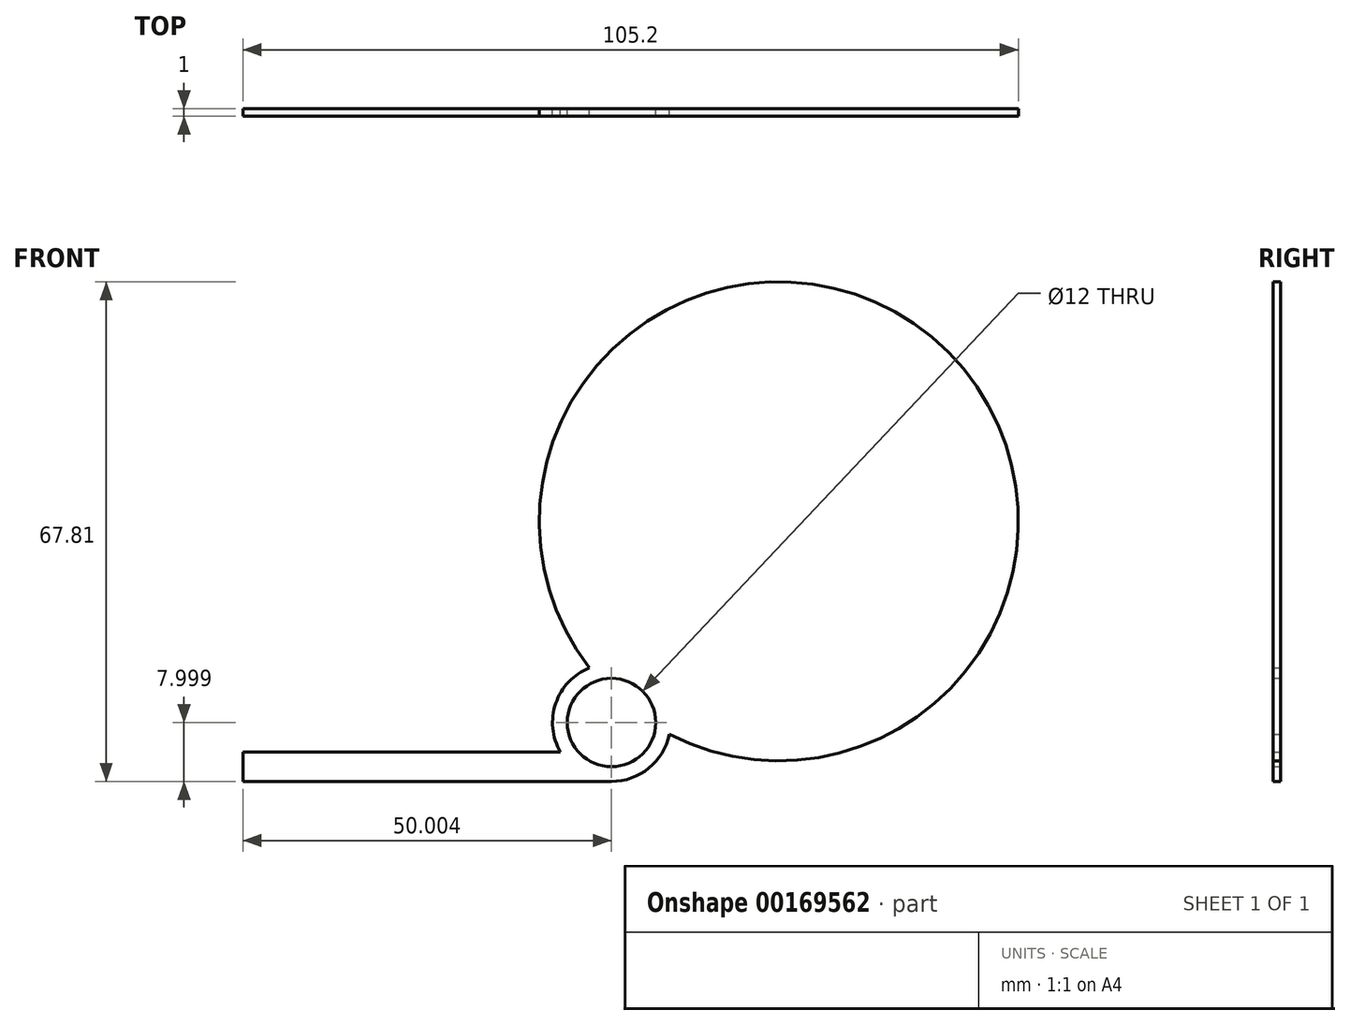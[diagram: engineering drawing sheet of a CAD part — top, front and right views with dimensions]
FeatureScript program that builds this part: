
annotation { "Feature Type Name" : "Feature", "Feature Type Description" : "" }
export const myFeature = defineFeature(function(context is Context, id is Id, definition is map)
    precondition{}
    {
        {
            var Q0;
            Q0=qCreatedBy(makeId("Front.planeOp"),FACE);
            var sketch = newSketch(context, id + "F0", { "sketchPlane" : qUnion([Q0])});
            skCircle(sketch, "E0", {"center": v(0, 0) * mm, "radius": 32.5 * mm});
            skLineSegment(sketch, "E1.bottom", {"start": v(-72.7, -31.31) * mm, "end": v(-22.7, -31.31) * mm});
            skLineSegment(sketch, "E1.top", {"start": v(-72.7, -35.31) * mm, "end": v(-22.7, -35.31) * mm});
            skLineSegment(sketch, "E1.left", {"start": v(-72.7, -31.31) * mm, "end": v(-72.7, -35.31) * mm});
            skLineSegment(sketch, "E1.right", {"start": v(-22.7, -31.31) * mm, "end": v(-22.7, -35.31) * mm});
            skLineSegment(sketch, "E2", {"start": v(0, 0) * mm, "end": v(-17.5, -30.31) * mm, "construction": true});
            skCircle(sketch, "E3", {"center": v(-22.7, -27.31) * mm, "radius": 6 * mm});
            skLineSegment(sketch, "E4", {"start": v(-72.7, -33.31) * mm, "end": v(-22.7, -33.31) * mm, "construction": true});
            skCircle(sketch, "E5", {"center": v(-22.7, -27.31) * mm, "radius": 8 * mm});
            skSolve(sketch);
        }
        {
            var Q0;
            Q0 = qSketchRegion(id + "F0", true);
            extrude(context, id + "F1", {"entities" : qUnion([Q0]), "depth" : 1 * mm});
        }
    });
